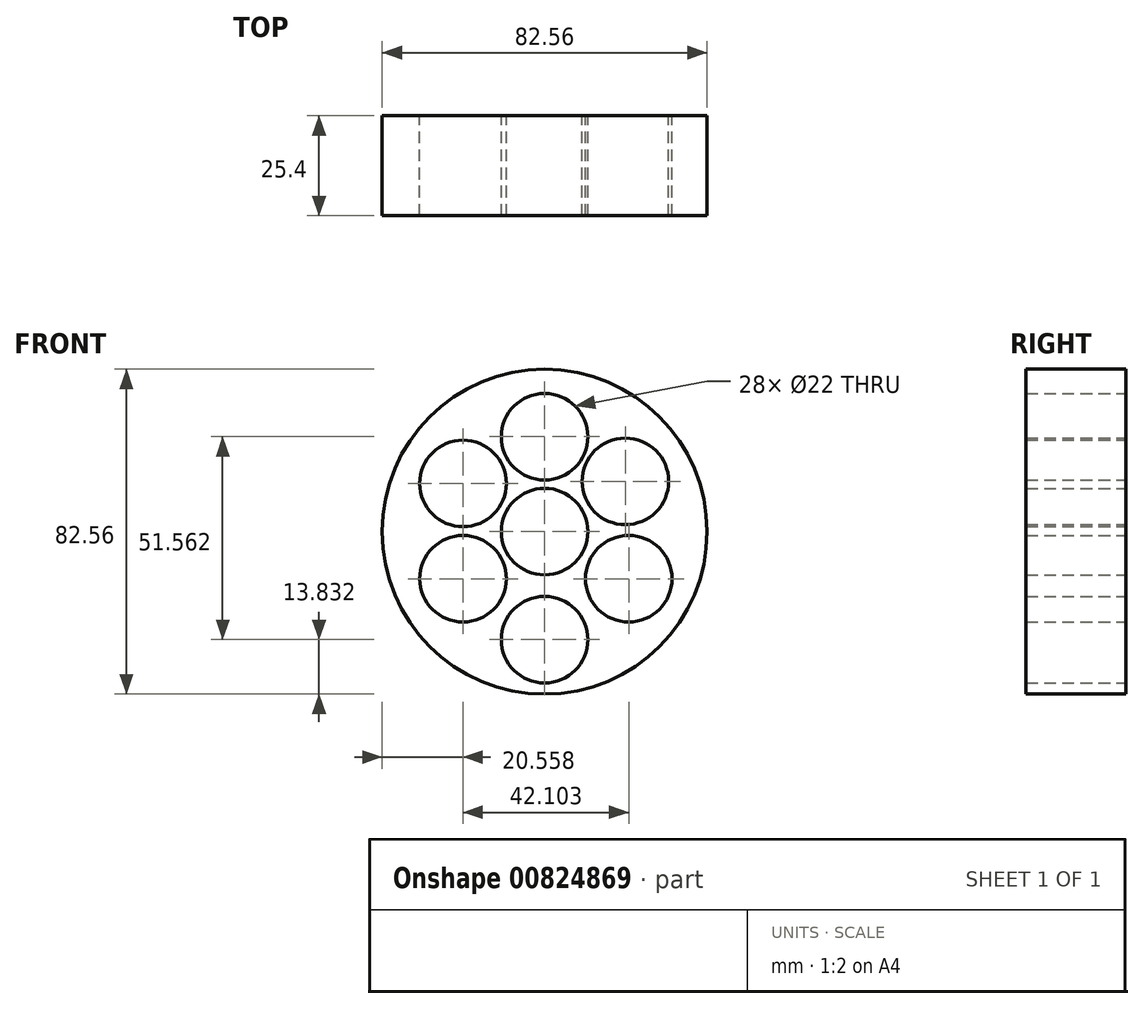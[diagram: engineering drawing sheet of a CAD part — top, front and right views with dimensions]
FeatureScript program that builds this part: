
annotation { "Feature Type Name" : "Feature", "Feature Type Description" : "" }
export const myFeature = defineFeature(function(context is Context, id is Id, definition is map)
    precondition{}
    {
        {
            var Q0;
            Q0=qCreatedBy(makeId("Front.planeOp"),FACE);
            var sketch = newSketch(context, id + "F0", { "sketchPlane" : qUnion([Q0])});
            skArc(sketch, "E0", {"start": v(2.43, 34.84) * mm, "mid": v(0, 34.92) * mm, "end": v(-2.43, 34.84) * mm});
            skPoint(sketch, "E1.center.orphan", {"position": v(0, 26.78) * mm});
            skPoint(sketch, "E2.center.orphan", {"position": v(-28.56, 0) * mm});
            skPoint(sketch, "E3.center.orphan", {"position": v(27.67, 0) * mm});
            skPoint(sketch, "E4.center.orphan", {"position": v(-27, 0) * mm});
            skPoint(sketch, "E5.center.orphan", {"position": v(0, -27.45) * mm});
            skCircle(sketch, "E6", {"center": v(0, 0) * mm, "radius": 11 * mm});
            skCircle(sketch, "E7", {"center": v(0, 0) * mm, "radius": 3.98 * mm});
            skPoint(sketch, "E8.center.orphan", {"position": v(0, 24.11) * mm});
            skCircle(sketch, "E9", {"center": v(0, 24.11) * mm, "radius": 11 * mm});
            skPoint(sketch, "E10.center.orphan", {"position": v(-20.72, 12.26) * mm});
            skCircle(sketch, "E11", {"center": v(-20.72, 12.26) * mm, "radius": 11 * mm});
            skPoint(sketch, "E12.center.orphan", {"position": v(-20.72, -11.96) * mm});
            skCircle(sketch, "E13", {"center": v(-20.72, -11.96) * mm, "radius": 11 * mm});
            skPoint(sketch, "E14.center.orphan", {"position": v(0, -22.11) * mm});
            skCircle(sketch, "E15", {"center": v(0, -27.45) * mm, "radius": 11 * mm});
            skPoint(sketch, "E16.center.orphan", {"position": v(21.38, -11.96) * mm});
            skCircle(sketch, "E17", {"center": v(21.38, -11.96) * mm, "radius": 11 * mm});
            skCircle(sketch, "E18", {"center": v(20.52, 12.78) * mm, "radius": 11 * mm});
            skPoint(sketch, "E19.start.orphan", {"position": v(-20.72, 28.11) * mm});
            skCircle(sketch, "E20", {"center": v(0, 0) * mm, "radius": 41.28 * mm});
            skSolve(sketch);
        }
        {
            var Q0;
            Q0 = qSketchRegion(id + "F0", true);
            extrude(context, id + "F1", {"entities" : qUnion([Q0]), "depth" : 25.4 * mm, "offsetDistance" : 25.4 * mm});
        }
    });
